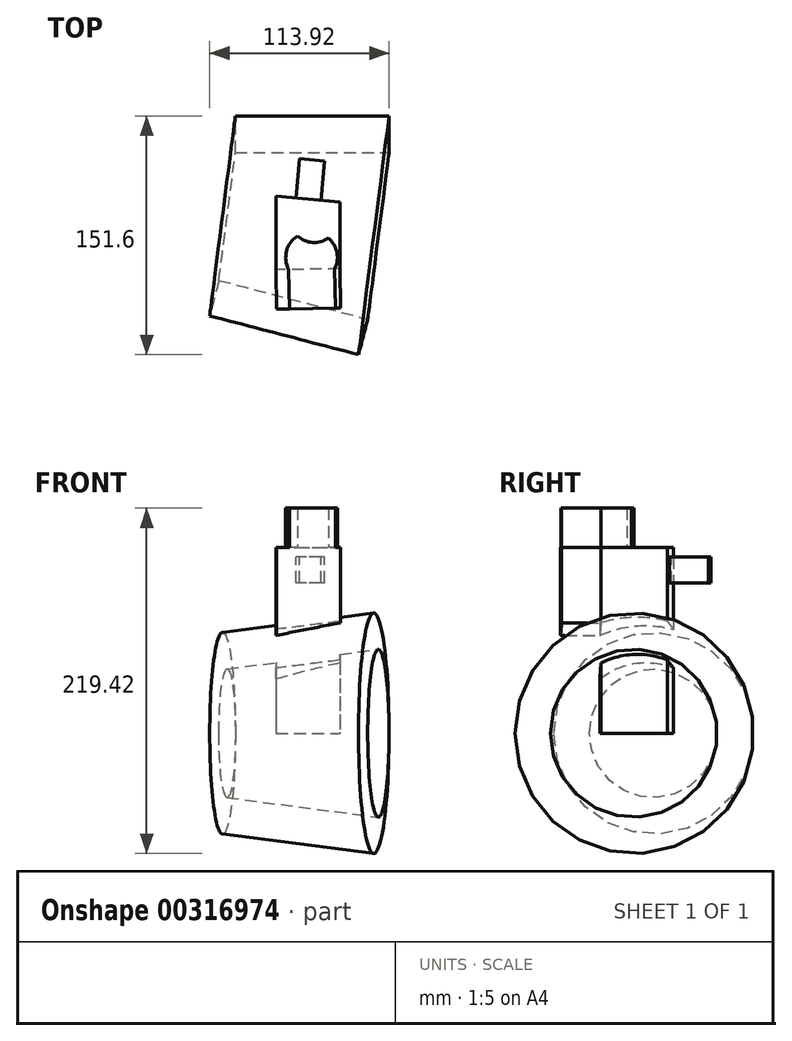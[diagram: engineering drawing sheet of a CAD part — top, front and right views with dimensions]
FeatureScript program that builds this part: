
annotation { "Feature Type Name" : "Feature", "Feature Type Description" : "" }
export const myFeature = defineFeature(function(context is Context, id is Id, definition is map)
    precondition{}
    {
        {
            var Q0;
            Q0=qCreatedBy(makeId("Top.planeOp"),FACE);
            var sketch = newSketch(context, id + "F0", { "sketchPlane" : qUnion([Q0])});
            skLineSegment(sketch, "E0", {"start": v(-18.13, -27.18) * mm, "end": v(67.57, -38.18) * mm});
            skLineSegment(sketch, "E1.bottom", {"start": v(-25.8, 38.32) * mm, "end": v(71.84, 38.32) * mm});
            skLineSegment(sketch, "E1.top", {"start": v(-25.8, 15.02) * mm, "end": v(71.84, 15.02) * mm});
            skLineSegment(sketch, "E1.left", {"start": v(-25.8, 38.32) * mm, "end": v(-25.8, 15.02) * mm});
            skLineSegment(sketch, "E1.right", {"start": v(71.84, 38.32) * mm, "end": v(71.84, 15.02) * mm});
            skSolve(sketch);
        }
        {
            var Q0;
            Q0=makeQuery(id+"F0.imprint","IMPRINT",FACE,{"disambiguationData":[TD([[makeQuery(id+"F0.imprint","IMPRINT",EDGE,{"derivedFrom":sQuery(id+"F0.wireOp",EDGE,"E1.bottom")}),-1.0]])]});
            var Q1;
            Q1=sQuery(id+"F0.wireOp",EDGE,"E0");
            revolve(context, id + "F1", {"entities" : qUnion([Q0]), "axis" : qUnion([Q1]), "revolveType" : RevolveType.FULL});
        }
        {
            var Q0;
            Q0=qCreatedBy(makeId("Top.planeOp"),FACE);
            var sketch = newSketch(context, id + "F2", { "sketchPlane" : qUnion([Q0])});
            skLineSegment(sketch, "E2", {"start": v(0, -59.4) * mm, "end": v(0, -12.56) * mm});
            skLineSegment(sketch, "E3", {"start": v(0, -12.56) * mm, "end": v(40.55, -16.44) * mm});
            skLineSegment(sketch, "E4", {"start": v(40.55, -16.44) * mm, "end": v(40.55, -58.68) * mm});
            skLineSegment(sketch, "E5", {"start": v(40.55, -58.68) * mm, "end": v(0, -59.4) * mm});
            skSolve(sketch);
        }
        {
            var Q0;
            Q0=makeQuery(id+"F2.imprint","IMPRINT",FACE,{"disambiguationData":[TD([[makeQuery(id+"F2.imprint","IMPRINT",EDGE,{"derivedFrom":sQuery(id+"F2.wireOp",EDGE,"E2")}),-1.0]])]});
            extrude(context, id + "F3", {"entities" : qUnion([Q0]), "operationType" : NewBodyOperationType.ADD, "depth" : 118 * mm});
        }
        {
            var Q0;
            Q0=makeQuery(id+"F3.opExtrude","CAP_FACE",FACE,{"disambiguationData":[OSD([sQuery(id+"F2.wireOp",EDGE,"E2"),sQuery(id+"F2.wireOp",EDGE,"E3"),sQuery(id+"F2.wireOp",EDGE,"E4"),sQuery(id+"F2.wireOp",EDGE,"E5")])],"isStart":false});
            var sketch = newSketch(context, id + "F4", { "sketchPlane" : qUnion([Q0])});
            skCircle(sketch, "E6", {"center": v(24.34, -26.4) * mm, "radius": 15.67 * mm});
            skCircle(sketch, "E7", {"center": v(22.6, -51.6) * mm, "radius": 16.37 * mm});
            skSolve(sketch);
        }
        {
            var Q0;
            {var subQ0=sQuery(id+"F4.wireOp",EDGE,"E7");var subQ1=sQuery(id+"F4.wireOp",EDGE,"E6");var subQ2=makeQuery(id+"F4.imprint","INTERSECT",VERTEX,{"disambiguationData":[OD(0.0)],"derivedFrom":[subQ1,subQ0]});Q0=makeQuery(id+"F4.imprint","IMPRINT",FACE,{"disambiguationData":[TD([[makeQuery(id+"F4.imprint","IMPRINT",EDGE,{"disambiguationData":[TD([[subQ2,-1.0]])],"derivedFrom":subQ1}),-1.0]])]});}
            extrude(context, id + "F5", {"entities" : qUnion([Q0]), "operationType" : NewBodyOperationType.ADD, "depth" : 25 * mm});
        }
        {
            var Q0;
            {var subQ0=sQuery(id+"F2.wireOp",EDGE,"E5");Q0=makeQuery(id+"F5.boolean.opBoolean","MERGE",FACE,{"derivedFrom":[makeQuery(id+"F3.boolean.opBoolean","SPLIT",FACE,{"disambiguationData":[TD([makeQuery(id+"F1.opRevolve","SWEPT_FACE",FACE,{"disambiguationData":[OSD([sQuery(id+"F0.wireOp",EDGE,"E1.bottom")])]})])],"derivedFrom":makeQuery(id+"F3.opExtrude","SWEPT_FACE",FACE,{"disambiguationData":[OSD([subQ0])]})}),makeQuery(id+"F5.opExtrude","SWEPT_FACE",FACE,{"disambiguationData":[OSD([subQ0])]})]});}
            var sketch = newSketch(context, id + "F6", { "sketchPlane" : qUnion([Q0])});
            skLineSegment(sketch, "E8.bottom", {"start": v(9.96, 100.62) * mm, "end": v(26.78, 100.62) * mm});
            skLineSegment(sketch, "E8.top", {"start": v(9.96, 80.06) * mm, "end": v(26.78, 80.06) * mm});
            skLineSegment(sketch, "E8.left", {"start": v(9.96, 100.62) * mm, "end": v(9.96, 80.06) * mm});
            skLineSegment(sketch, "E8.right", {"start": v(26.78, 100.62) * mm, "end": v(26.78, 80.06) * mm});
            skLineSegment(sketch, "E9.bottom", {"start": v(20.33, 131.25) * mm, "end": v(32.8, 131.25) * mm});
            skLineSegment(sketch, "E9.top", {"start": v(20.33, 107.47) * mm, "end": v(32.8, 107.47) * mm});
            skLineSegment(sketch, "E9.left", {"start": v(20.33, 131.25) * mm, "end": v(20.33, 107.47) * mm});
            skLineSegment(sketch, "E9.right", {"start": v(32.8, 131.25) * mm, "end": v(32.8, 107.47) * mm});
            skLineSegment(sketch, "E10.bottom", {"start": v(10.77, 126.46) * mm, "end": v(14.6, 126.46) * mm});
            skLineSegment(sketch, "E10.top", {"start": v(10.77, 107.47) * mm, "end": v(14.6, 107.47) * mm});
            skLineSegment(sketch, "E10.left", {"start": v(10.77, 126.46) * mm, "end": v(10.77, 107.47) * mm});
            skLineSegment(sketch, "E10.right", {"start": v(14.6, 126.46) * mm, "end": v(14.6, 107.47) * mm});
            skSolve(sketch);
        }
        {
            var Q0;
            Q0=makeQuery(id+"F6.imprint","IMPRINT",FACE,{"disambiguationData":[TD([[makeQuery(id+"F6.imprint","IMPRINT",EDGE,{"derivedFrom":sQuery(id+"F6.wireOp",EDGE,"E9.bottom")}),-1.0]])]});
            extrude(context, id + "F7", {"entities" : qUnion([Q0]), "operationType" : NewBodyOperationType.ADD, "depth" : 25 * mm});
        }
        {
            var Q0;
            Q0 = qSketchRegion(id + "F6", true);
            var Q1;
            {var subQ0=sQuery(id+"F2.wireOp",EDGE,"E5");Q1=makeQuery(id+"F5.boolean.opBoolean","MERGE",FACE,{"derivedFrom":[makeQuery(id+"F3.boolean.opBoolean","SPLIT",FACE,{"disambiguationData":[TD([makeQuery(id+"F1.opRevolve","SWEPT_FACE",FACE,{"disambiguationData":[OSD([sQuery(id+"F0.wireOp",EDGE,"E1.bottom")])]})])],"derivedFrom":makeQuery(id+"F3.opExtrude","SWEPT_FACE",FACE,{"disambiguationData":[OSD([subQ0])]})}),makeQuery(id+"F5.opExtrude","SWEPT_FACE",FACE,{"disambiguationData":[OSD([subQ0])]})]});}
            extrude(context, id + "F8", {"entities" : qUnion([Q0, Q1]), "operationType" : NewBodyOperationType.ADD, "depth" : 25 * mm});
        }
        {
            var Q0;
            {var subQ1=sQuery(id+"F2.wireOp",EDGE,"E3");Q0=makeQuery(id+"F3.boolean.opBoolean","SPLIT",FACE,{"disambiguationData":[TD([makeQuery(id+"F1.opRevolve","SWEPT_FACE",FACE,{"disambiguationData":[OSD([sQuery(id+"F0.wireOp",EDGE,"E1.bottom")])]})])],"derivedFrom":makeQuery(id+"F3.opExtrude","SWEPT_FACE",FACE,{"disambiguationData":[OSD([subQ1])]})});}
            var sketch = newSketch(context, id + "F9", { "sketchPlane" : qUnion([Q0])});
            skLineSegment(sketch, "E11.bottom", {"start": v(-29.83, 95.54) * mm, "end": v(-13.92, 95.54) * mm});
            skLineSegment(sketch, "E11.top", {"start": v(-29.83, 112) * mm, "end": v(-13.92, 112) * mm});
            skLineSegment(sketch, "E11.left", {"start": v(-29.83, 95.54) * mm, "end": v(-29.83, 112) * mm});
            skLineSegment(sketch, "E11.right", {"start": v(-13.92, 95.54) * mm, "end": v(-13.92, 112) * mm});
            skSolve(sketch);
        }
        {
            var Q0;
            Q0=makeQuery(id+"F9.imprint","IMPRINT",FACE,{"disambiguationData":[TD([[makeQuery(id+"F9.imprint","IMPRINT",EDGE,{"derivedFrom":sQuery(id+"F9.wireOp",EDGE,"E11.bottom")}),1.0]])]});
            extrude(context, id + "F10", {"entities" : qUnion([Q0]), "operationType" : NewBodyOperationType.ADD, "depth" : 25 * mm});
        }
    });
